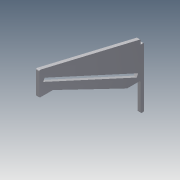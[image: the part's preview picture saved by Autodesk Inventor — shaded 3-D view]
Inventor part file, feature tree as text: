
AUTODESK INVENTOR PART (.ipt)
format: ipt  version: 2014 (Build 180170000, 170)  size: 120,832 bytes
history: native  units: mm
features: extrude x3, sketch x3, fillet x1
ambient origin geometry x8: Origin, YZ Plane, XZ Plane, XY Plane, X Axis, Y Axis, Z Axis, Center Point
bodies: Solid1 (feature_tree)
feature tree (7):
  extrude  "Extrusion1"  Depth=65.0mm
  extrude  "Extrusion3"  Depth=6.0mm TaperAngle=0.0deg
  extrude  "Extrusion4"  Depth=25.0mm
  fillet  "Fillet1"  Radius=8.1mm
  sketch  "Sketch1"  dims[d0=25.0mm d1=65.0mm]
  sketch  "Sketch3"  dims[d2=185.0mm d3=6.0mm d4=0.0mm]
  sketch  "Sketch4"  dims[d10=25.0mm d11=25.0mm d12=8.1mm d14=6.0mm d15=6.0mm d16=0.0mm d17=25.0mm d20=25.0mm d21=108.8mm d23=185.0mm d24=85.0mm d28=8.0mm d29=8.0mm d30=6.0mm d31=0.0mm d32=6.0mm d33=2.0mm]
